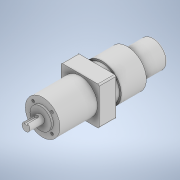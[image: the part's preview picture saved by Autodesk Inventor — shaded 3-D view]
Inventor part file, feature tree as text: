
AUTODESK INVENTOR PART (.ipt)
format: ipt  version: 2020 (Build 240168000, 168)  size: 250,880 bytes
history: native  units: mm
features: sketch x11, extrude x10, projected_geometry x3, fillet x2, other x1, hole x1
ambient origin geometry x8: Origin, YZ Plane, XZ Plane, XY Plane, X Axis, Y Axis, Z Axis, Center Point
bodies: Body1 (feature_tree)
feature tree (28):
  other  "솔리드1"
  extrude  "돌출1"  Depth=57.0mm
  extrude  "돌출2"  Depth=57.0mm
  extrude  "돌출5"  Depth=2.0mm
  extrude  "돌출6"  Depth=25.0mm TaperAngle=0.0deg
  extrude  "돌출7"  Depth=52.0mm
  extrude  "돌출8"  Depth=56.1mm TaperAngle=0.0deg
  extrude  "돌출9"  Depth=32.0mm
  extrude  "돌출10"  Depth=30.0mm
  fillet  "모깎기1"  Radius=32.0mm
  sketch  "스케치10"
  extrude  "돌출11"  Depth=3.0mm TaperAngle=0.0deg
  fillet  "모깎기2"  Radius=12.0mm
  extrude  "돌출12"  Depth=22.0mm TaperAngle=0.0deg
  hole  "구멍1"  [1 undecoded]
  sketch  "스케치1"
  sketch  "스케치2"
  sketch  "스케치4"
  sketch  "스케치5"
  sketch  "스케치6"
  projected_geometry  "투영된 루프1"
  sketch  "스케치7"
  projected_geometry  "투영된 루프2"
  sketch  "스케치8"
  sketch  "스케치9"
  sketch  "스케치11"
  projected_geometry  "투영된 루프3"
  sketch  "스케치13"
note: 1 required parameter value undecoded (feature->parameter linkage not recoverable at this tier; creation-order binding heuristic only, values carry confidence <= 0.55)
